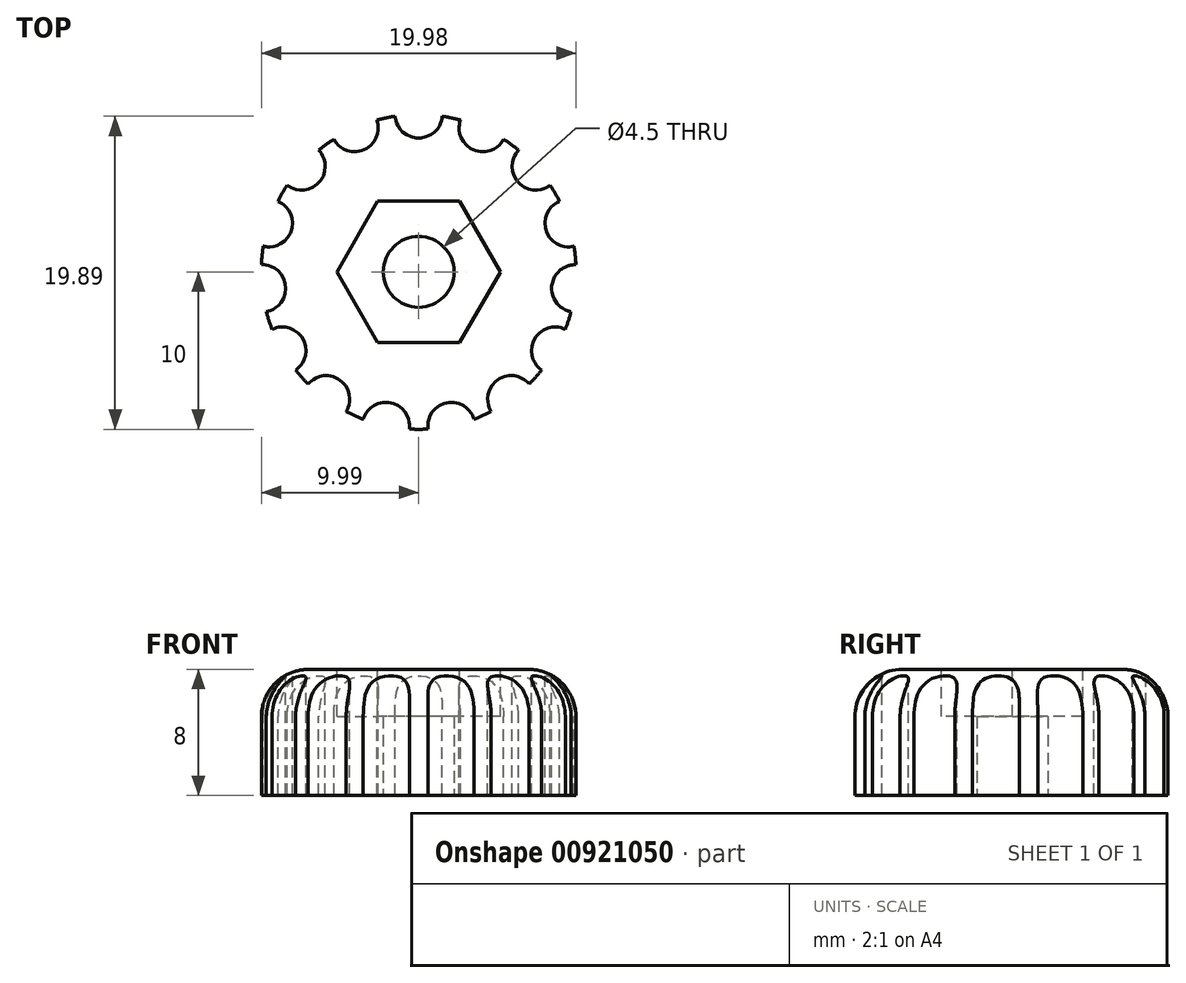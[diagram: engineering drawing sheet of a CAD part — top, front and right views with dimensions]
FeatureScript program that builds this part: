
annotation { "Feature Type Name" : "Feature", "Feature Type Description" : "" }
export const myFeature = defineFeature(function(context is Context, id is Id, definition is map)
    precondition{}
    {
        {
            var Q0;
            Q0=qCreatedBy(makeId("Top.planeOp"),FACE);
            var sketch = newSketch(context, id + "F0", { "sketchPlane" : qUnion([Q0])});
            skCircle(sketch, "E0", {"center": v(0, 0) * mm, "radius": 10 * mm});
            skCircle(sketch, "E1", {"center": v(0, 0) * mm, "radius": 2.25 * mm});
            skSolve(sketch);
        }
        {
            var Q0;
            Q0=makeQuery(id+"F0.imprint","IMPRINT",FACE,{"disambiguationData":[TD([[makeQuery(id+"F0.imprint","IMPRINT",EDGE,{"derivedFrom":sQuery(id+"F0.wireOp",EDGE,"E0")}),1.0]])]});
            extrude(context, id + "F1", {"entities" : qUnion([Q0]), "depth" : 8 * mm, "offsetDistance" : 25 * mm});
        }
        {
            var Q0;
            Q0=makeQuery(id+"F1.opExtrude","CAP_FACE",FACE,{"disambiguationData":[OSD([sQuery(id+"F0.wireOp",EDGE,"E0"),sQuery(id+"F0.wireOp",EDGE,"E1")])],"isStart":false});
            var sketch = newSketch(context, id + "F2", { "sketchPlane" : qUnion([Q0])});
            skSolve(sketch);
        }
        {
            var Q0;
            Q0=makeQuery(id+"F2.imprint","IMPRINT",FACE,{"disambiguationData":[TD([[makeQuery(id+"F2.imprint","IMPRINT",EDGE,{"derivedFrom":makeQuery(id+"F1.opExtrude","CAP_EDGE",EDGE,{"disambiguationData":[OSD([sQuery(id+"F0.wireOp",EDGE,"E0")])],"isStart":false})}),1.0]])]});
            var sketch = newSketch(context, id + "F3", { "sketchPlane" : qUnion([Q0])});
            skCircle(sketch, "E2.cCircle", {"center": v(0, 0) * mm, "radius": 4.5 * mm, "construction": true});
            skLineSegment(sketch, "E2.0", {"start": v(2.6, -4.5) * mm, "end": v(-2.6, -4.5) * mm});
            skLineSegment(sketch, "E2.1", {"start": v(-2.6, -4.5) * mm, "end": v(-5.2, 0) * mm});
            skLineSegment(sketch, "E2.2", {"start": v(-5.2, 0) * mm, "end": v(-2.6, 4.5) * mm});
            skLineSegment(sketch, "E2.3", {"start": v(-2.6, 4.5) * mm, "end": v(2.6, 4.5) * mm});
            skLineSegment(sketch, "E2.4", {"start": v(2.6, 4.5) * mm, "end": v(5.2, 0) * mm});
            skLineSegment(sketch, "E2.5", {"start": v(5.2, 0) * mm, "end": v(2.6, -4.5) * mm});
            skPoint(sketch, "E2.0.midPoint", {"position": v(0, -4.5) * mm});
            skSolve(sketch);
        }
        {
            var Q0;
            Q0 = qSketchRegion(id + "F3", true);
            extrude(context, id + "F4", {"entities" : qUnion([Q0]), "operationType" : NewBodyOperationType.REMOVE, "oppositeDirection" : true, "depth" : 3 * mm, "offsetDistance" : 25 * mm});
        }
        {
            var Q0;
            Q0=makeQuery(id+"F1.opExtrude","CAP_EDGE",EDGE,{"disambiguationData":[OSD([sQuery(id+"F0.wireOp",EDGE,"E0")])],"isStart":false});
            fillet(context, id + "F5", {"entities" : qUnion([Q0]), "radius" : 3 * mm, "tangentPropagation" : true, "allowEdgeOverflow" : false});
        }
        {
            var Q0;
            Q0=makeQuery(id+"F1.opExtrude","CAP_FACE",FACE,{"disambiguationData":[OSD([sQuery(id+"F0.wireOp",EDGE,"E0"),sQuery(id+"F0.wireOp",EDGE,"E1")])],"isStart":false});
            var sketch = newSketch(context, id + "F6", { "sketchPlane" : qUnion([Q0])});
            skCircle(sketch, "E3.0", {"center": v(0, 0) * mm, "radius": 10 * mm});
            skCircle(sketch, "E4", {"center": v(0, 10) * mm, "radius": 1.5 * mm});
            skCircle(sketch, "E5.1.0", {"center": v(-4.07, 9.14) * mm, "radius": 1.5 * mm});
            skCircle(sketch, "E5.2.0", {"center": v(-7.43, 6.7) * mm, "radius": 1.5 * mm});
            skCircle(sketch, "E5.3.0", {"center": v(-9.51, 3.1) * mm, "radius": 1.5 * mm});
            skCircle(sketch, "E5.4.0", {"center": v(-9.95, -1.05) * mm, "radius": 1.5 * mm});
            skCircle(sketch, "E5.5.0", {"center": v(-8.66, -5) * mm, "radius": 1.5 * mm});
            skCircle(sketch, "E5.6.0", {"center": v(-5.88, -8.1) * mm, "radius": 1.5 * mm});
            skCircle(sketch, "E5.7.0", {"center": v(-2.08, -9.78) * mm, "radius": 1.5 * mm});
            skCircle(sketch, "E5.8.0", {"center": v(2.08, -9.78) * mm, "radius": 1.5 * mm});
            skCircle(sketch, "E5.9.0", {"center": v(5.88, -8.1) * mm, "radius": 1.5 * mm});
            skCircle(sketch, "E5.10.0", {"center": v(8.66, -5) * mm, "radius": 1.5 * mm});
            skCircle(sketch, "E5.11.0", {"center": v(9.95, -1.05) * mm, "radius": 1.5 * mm});
            skCircle(sketch, "E5.12.0", {"center": v(9.51, 3.1) * mm, "radius": 1.5 * mm});
            skCircle(sketch, "E5.13.0", {"center": v(7.43, 6.7) * mm, "radius": 1.5 * mm});
            skCircle(sketch, "E5.14.0", {"center": v(4.07, 9.14) * mm, "radius": 1.5 * mm});
            skSolve(sketch);
        }
        {
            var Q0;
            {var subQ0=sQuery(id+"F6.wireOp",EDGE,"E5.3.0");var subQ1=sQuery(id+"F6.wireOp",EDGE,"E3.0");var subQ2=makeQuery(id+"F6.imprint","INTERSECT",VERTEX,{"disambiguationData":[OD(0.0)],"derivedFrom":[subQ1,subQ0]});Q0=makeQuery(id+"F6.imprint","IMPRINT",FACE,{"disambiguationData":[TD([[makeQuery(id+"F6.imprint","IMPRINT",EDGE,{"disambiguationData":[TD([[subQ2,-1.0]])],"derivedFrom":subQ1}),1.0]])]});}
            var Q1;
            {var subQ0=sQuery(id+"F6.wireOp",EDGE,"E5.2.0");var subQ1=sQuery(id+"F6.wireOp",EDGE,"E3.0");var subQ2=makeQuery(id+"F6.imprint","INTERSECT",VERTEX,{"disambiguationData":[OD(0.0)],"derivedFrom":[subQ1,subQ0]});Q1=makeQuery(id+"F6.imprint","IMPRINT",FACE,{"disambiguationData":[TD([[makeQuery(id+"F6.imprint","IMPRINT",EDGE,{"disambiguationData":[TD([[subQ2,-1.0]])],"derivedFrom":subQ1}),1.0]])]});}
            var Q2;
            {var subQ0=sQuery(id+"F6.wireOp",EDGE,"E5.5.0");var subQ1=sQuery(id+"F6.wireOp",EDGE,"E3.0");var subQ2=makeQuery(id+"F6.imprint","INTERSECT",VERTEX,{"disambiguationData":[OD(0.0)],"derivedFrom":[subQ1,subQ0]});Q2=makeQuery(id+"F6.imprint","IMPRINT",FACE,{"disambiguationData":[TD([[makeQuery(id+"F6.imprint","IMPRINT",EDGE,{"disambiguationData":[TD([[subQ2,-1.0]])],"derivedFrom":subQ1}),1.0]])]});}
            var Q3;
            {var subQ0=sQuery(id+"F6.wireOp",EDGE,"E5.4.0");var subQ1=sQuery(id+"F6.wireOp",EDGE,"E3.0");var subQ2=makeQuery(id+"F6.imprint","INTERSECT",VERTEX,{"disambiguationData":[OD(0.0)],"derivedFrom":[subQ1,subQ0]});Q3=makeQuery(id+"F6.imprint","IMPRINT",FACE,{"disambiguationData":[TD([[makeQuery(id+"F6.imprint","IMPRINT",EDGE,{"disambiguationData":[TD([[subQ2,-1.0]])],"derivedFrom":subQ1}),1.0]])]});}
            var Q4;
            {var subQ0=sQuery(id+"F6.wireOp",EDGE,"E5.6.0");var subQ1=sQuery(id+"F6.wireOp",EDGE,"E3.0");var subQ2=makeQuery(id+"F6.imprint","INTERSECT",VERTEX,{"disambiguationData":[OD(0.0)],"derivedFrom":[subQ1,subQ0]});Q4=makeQuery(id+"F6.imprint","IMPRINT",FACE,{"disambiguationData":[TD([[makeQuery(id+"F6.imprint","IMPRINT",EDGE,{"disambiguationData":[TD([[subQ2,-1.0]])],"derivedFrom":subQ1}),1.0]])]});}
            var Q5;
            {var subQ0=sQuery(id+"F6.wireOp",EDGE,"E5.7.0");var subQ1=sQuery(id+"F6.wireOp",EDGE,"E3.0");var subQ2=makeQuery(id+"F6.imprint","INTERSECT",VERTEX,{"disambiguationData":[OD(0.0)],"derivedFrom":[subQ1,subQ0]});Q5=makeQuery(id+"F6.imprint","IMPRINT",FACE,{"disambiguationData":[TD([[makeQuery(id+"F6.imprint","IMPRINT",EDGE,{"disambiguationData":[TD([[subQ2,-1.0]])],"derivedFrom":subQ1}),1.0]])]});}
            var Q6;
            {var subQ0=sQuery(id+"F6.wireOp",EDGE,"E5.8.0");var subQ1=sQuery(id+"F6.wireOp",EDGE,"E3.0");var subQ2=makeQuery(id+"F6.imprint","INTERSECT",VERTEX,{"disambiguationData":[OD(0.0)],"derivedFrom":[subQ1,subQ0]});Q6=makeQuery(id+"F6.imprint","IMPRINT",FACE,{"disambiguationData":[TD([[makeQuery(id+"F6.imprint","IMPRINT",EDGE,{"disambiguationData":[TD([[subQ2,-1.0]])],"derivedFrom":subQ1}),1.0]])]});}
            var Q7;
            {var subQ0=sQuery(id+"F6.wireOp",EDGE,"E5.9.0");var subQ1=sQuery(id+"F6.wireOp",EDGE,"E3.0");var subQ2=makeQuery(id+"F6.imprint","INTERSECT",VERTEX,{"disambiguationData":[OD(0.0)],"derivedFrom":[subQ1,subQ0]});Q7=makeQuery(id+"F6.imprint","IMPRINT",FACE,{"disambiguationData":[TD([[makeQuery(id+"F6.imprint","IMPRINT",EDGE,{"disambiguationData":[TD([[subQ2,-1.0]])],"derivedFrom":subQ1}),1.0]])]});}
            var Q8;
            {var subQ0=sQuery(id+"F6.wireOp",EDGE,"E5.10.0");var subQ1=sQuery(id+"F6.wireOp",EDGE,"E3.0");var subQ2=makeQuery(id+"F6.imprint","INTERSECT",VERTEX,{"disambiguationData":[OD(0.0)],"derivedFrom":[subQ1,subQ0]});Q8=makeQuery(id+"F6.imprint","IMPRINT",FACE,{"disambiguationData":[TD([[makeQuery(id+"F6.imprint","IMPRINT",EDGE,{"disambiguationData":[TD([[subQ2,-1.0]])],"derivedFrom":subQ1}),1.0]])]});}
            var Q9;
            {var subQ0=sQuery(id+"F6.wireOp",EDGE,"E5.11.0");var subQ1=sQuery(id+"F6.wireOp",EDGE,"E3.0");var subQ2=makeQuery(id+"F6.imprint","INTERSECT",VERTEX,{"disambiguationData":[OD(0.0)],"derivedFrom":[subQ1,subQ0]});Q9=makeQuery(id+"F6.imprint","IMPRINT",FACE,{"disambiguationData":[TD([[makeQuery(id+"F6.imprint","IMPRINT",EDGE,{"disambiguationData":[TD([[subQ2,1.0]])],"derivedFrom":subQ1}),1.0]])]});}
            var Q10;
            {var subQ0=sQuery(id+"F6.wireOp",EDGE,"E5.12.0");var subQ1=sQuery(id+"F6.wireOp",EDGE,"E3.0");var subQ2=makeQuery(id+"F6.imprint","INTERSECT",VERTEX,{"disambiguationData":[OD(0.0)],"derivedFrom":[subQ1,subQ0]});Q10=makeQuery(id+"F6.imprint","IMPRINT",FACE,{"disambiguationData":[TD([[makeQuery(id+"F6.imprint","IMPRINT",EDGE,{"disambiguationData":[TD([[subQ2,-1.0]])],"derivedFrom":subQ1}),1.0]])]});}
            var Q11;
            {var subQ0=sQuery(id+"F6.wireOp",EDGE,"E5.13.0");var subQ1=sQuery(id+"F6.wireOp",EDGE,"E3.0");var subQ2=makeQuery(id+"F6.imprint","INTERSECT",VERTEX,{"disambiguationData":[OD(0.0)],"derivedFrom":[subQ1,subQ0]});Q11=makeQuery(id+"F6.imprint","IMPRINT",FACE,{"disambiguationData":[TD([[makeQuery(id+"F6.imprint","IMPRINT",EDGE,{"disambiguationData":[TD([[subQ2,-1.0]])],"derivedFrom":subQ1}),1.0]])]});}
            var Q12;
            {var subQ0=sQuery(id+"F6.wireOp",EDGE,"E5.14.0");var subQ1=sQuery(id+"F6.wireOp",EDGE,"E3.0");var subQ2=makeQuery(id+"F6.imprint","INTERSECT",VERTEX,{"disambiguationData":[OD(0.0)],"derivedFrom":[subQ1,subQ0]});Q12=makeQuery(id+"F6.imprint","IMPRINT",FACE,{"disambiguationData":[TD([[makeQuery(id+"F6.imprint","IMPRINT",EDGE,{"disambiguationData":[TD([[subQ2,-1.0]])],"derivedFrom":subQ1}),1.0]])]});}
            var Q13;
            {var subQ0=sQuery(id+"F6.wireOp",EDGE,"E4");var subQ1=sQuery(id+"F6.wireOp",EDGE,"E3.0");var subQ2=makeQuery(id+"F6.imprint","INTERSECT",VERTEX,{"disambiguationData":[OD(0.0)],"derivedFrom":[subQ1,subQ0]});Q13=makeQuery(id+"F6.imprint","IMPRINT",FACE,{"disambiguationData":[TD([[makeQuery(id+"F6.imprint","IMPRINT",EDGE,{"disambiguationData":[TD([[subQ2,-1.0]])],"derivedFrom":subQ1}),1.0]])]});}
            var Q14;
            {var subQ0=sQuery(id+"F6.wireOp",EDGE,"E5.1.0");var subQ1=sQuery(id+"F6.wireOp",EDGE,"E3.0");var subQ2=makeQuery(id+"F6.imprint","INTERSECT",VERTEX,{"disambiguationData":[OD(0.0)],"derivedFrom":[subQ1,subQ0]});Q14=makeQuery(id+"F6.imprint","IMPRINT",FACE,{"disambiguationData":[TD([[makeQuery(id+"F6.imprint","IMPRINT",EDGE,{"disambiguationData":[TD([[subQ2,-1.0]])],"derivedFrom":subQ1}),1.0]])]});}
            extrude(context, id + "F7", {"entities" : qUnion([Q0, Q1, Q2, Q3, Q4, Q5, Q6, Q7, Q8, Q9, Q10, Q11, Q12, Q13, Q14]), "operationType" : NewBodyOperationType.REMOVE, "oppositeDirection" : true, "depth" : 25 * mm, "offsetDistance" : 25 * mm});
        }
    });
